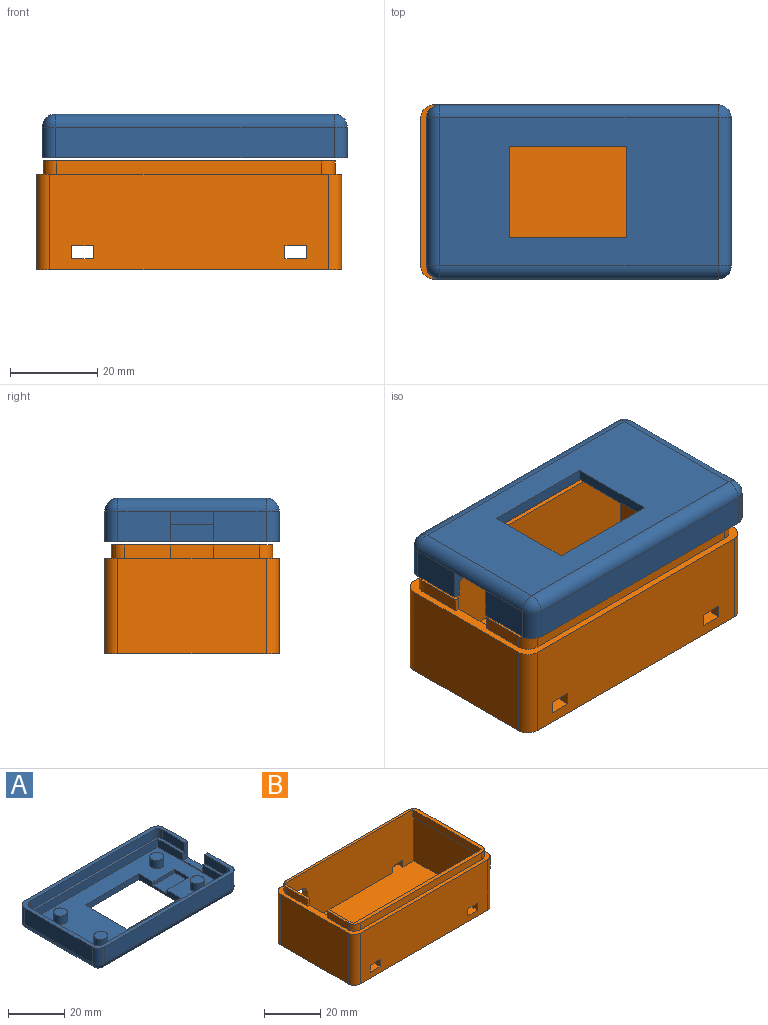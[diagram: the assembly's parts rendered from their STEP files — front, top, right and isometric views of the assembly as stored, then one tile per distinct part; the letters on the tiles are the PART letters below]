
ASSEMBLY  parts=2 mates=1
PART A: 53 faces, bbox 70x40x10 mm
  f0: plane 70x40mm, normal (0,0,1), area 293.4mm2, adj f9,f10,f11,f15,f16,f17,f18,f26
  f1: plane 35x3.5mm, normal (1,0,0), area 122.5mm2, adj f2,f4,f12,f39
  f2: plane 65x3.5mm, normal (0,1,0), area 227.5mm2, adj f1,f3,f12,f39
  f3: plane 35x3.5mm, normal (-1,0,0), area 92.5mm2, adj f2,f4,f9,f10,f12,f38,f39
  f4: plane 65x3.5mm, normal (0,-1,0), area 227.5mm2, adj f1,f3,f12,f39
  f5: cylinder r=2.5mm len=5mm, axis (0,0,-1), area 55mm2, adj f12,f52
  f6: cylinder r=2.5mm len=5mm, axis (0,0,-1), area 55mm2, adj f12,f51
  f7: cylinder r=2.5mm len=5mm, axis (0,0,-1), area 55mm2, adj f12,f50
  f8: cylinder r=2.5mm len=5mm, axis (0,0,-1), area 55mm2, adj f12,f49
  f9: plane 7x2.5mm, normal (0,1,0), area 13.1mm2, adj f0,f3,f11,f38,f39,f41
  f10: plane 7x2.5mm, normal (0,-1,0), area 13.1mm2, adj f0,f3,f17,f38,f39,f40
  f11: plane 12x7mm, normal (1,0,0), area 84mm2, adj f0,f9,f28,f29
  f12: plane 65x35mm, normal (0,0,1), area 1552.5mm2, adj f1,f2,f3,f4,f5,f6,f7,f8
  f13: plane 21x2.5mm, normal (-1,0,0), area 42mm2, adj f12,f14,f19,f21,f22,f23,f25
  f14: plane 64x34mm, normal (0,0,-1), area 1609mm2, adj f13,f19,f20,f21,f29,f30,f34,f35
  f15: plane 34x7mm, normal (-1,0,0), area 238mm2, adj f0,f31,f35,f37
  f16: plane 64x7mm, normal (0,-1,0), area 448mm2, adj f0,f28,f34,f37
  f17: plane 12x7mm, normal (1,0,0), area 84mm2, adj f0,f10,f26,f29
  f18: plane 64x7mm, normal (0,1,0), area 448mm2, adj f0,f26,f30,f31
  f19: plane 27x2.5mm, normal (0,-1,0), area 67.5mm2, adj f12,f13,f14,f20
  f20: plane 21x2.5mm, normal (1,0,0), area 52.5mm2, adj f12,f14,f19,f21
  f21: plane 27x2.5mm, normal (0,1,0), area 67.5mm2, adj f12,f13,f14,f20
  f22: plane 11x1.5mm, normal (0,-1,0), area 16.5mm2, adj f12,f13,f24,f25
  f23: plane 11x1.5mm, normal (0,1,0), area 16.5mm2, adj f12,f13,f24,f25
  f24: plane 7x1.5mm, normal (-1,0,0), area 10.5mm2, adj f12,f22,f23,f25
  f25: plane 11x7mm, normal (0,0,1), area 77mm2, adj f13,f22,f23,f24
  f26: cylinder r=3mm len=7mm, axis (0,0,1), area 33mm2, adj f0,f17,f18,f27
  f27: sphere r=3mm, area 14.1mm2, adj f26,f29,f30
  f28: cylinder r=3mm len=7mm, axis (0,0,-1), area 33mm2, adj f0,f11,f16,f32
  f29: cylinder r=3mm len=34mm, axis (0,1,0), area 160.2mm2, adj f11,f14,f17,f27,f32,f38
  f30: cylinder r=3mm len=64mm, axis (-1,0,0), area 301.6mm2, adj f14,f18,f27,f33
  f31: cylinder r=3mm len=7mm, axis (0,0,-1), area 33mm2, adj f0,f15,f18,f33
  f32: sphere r=3mm, area 14.1mm2, adj f28,f29,f34
  f33: sphere r=3mm, area 14.1mm2, adj f30,f31,f35
  f34: cylinder r=3mm len=64mm, axis (1,0,0), area 301.6mm2, adj f14,f16,f32,f36
  f35: cylinder r=3mm len=34mm, axis (0,-1,0), area 160.2mm2, adj f14,f15,f33,f36
  f36: sphere r=3mm, area 14.1mm2, adj f34,f35,f37
  f37: cylinder r=3mm len=7mm, axis (0,0,1), area 33mm2, adj f0,f15,f16,f36
  f38: plane 10x2.5mm, normal (0,0,1), area 25mm2, adj f3,f9,f10,f29
  f39: plane 67.1x37.1mm, normal (0,0,1), area 198.9mm2, adj f1,f2,f3,f4,f9,f10,f40,f41
  f40: plane 11.5x4mm, normal (-1,0,0), area 46mm2, adj f0,f10,f39,f48
  f41: plane 11.6x4mm, normal (-1,0,0), area 46.4mm2, adj f0,f9,f39,f42
  f42: cylinder r=2mm len=4mm, axis (0,0,1), area 12.6mm2, adj f0,f39,f41,f43
  f43: plane 63.1x4mm, normal (0,1,0), area 252.4mm2, adj f0,f39,f42,f44
  f44: cylinder r=2mm len=4mm, axis (0,0,1), area 12.6mm2, adj f0,f39,f43,f45
  f45: plane 32.1x4mm, normal (1,0,0), area 128.4mm2, adj f0,f39,f44,f46
  f46: cylinder r=3mm len=4mm, axis (0,0,1), area 18.8mm2, adj f0,f39,f45,f47
  f47: plane 62.1x4mm, normal (0,-1,0), area 248.4mm2, adj f0,f39,f46,f48
  f48: cylinder r=2mm len=4mm, axis (0,0,1), area 12.6mm2, adj f0,f39,f40,f47
  f49: plane 5x5mm, normal (0,0,1), area 19.6mm2, adj f8
  f50: plane 5x5mm, normal (0,0,1), area 19.6mm2, adj f7
  f51: plane 5x5mm, normal (0,0,1), area 19.6mm2, adj f6
  f52: plane 5x5mm, normal (0,0,1), area 19.6mm2, adj f5
PART B: 43 faces, bbox 70x40x25 mm
  f0: plane 10.5x3mm, normal (-1,0,0), area 31.5mm2, adj f1,f6,f28,f42
  f1: plane 67x37mm, normal (0,0,1), area 236mm2, adj f0,f5,f10,f19,f20,f21,f22,f23
  f2: plane 64x22mm, normal (0,-1,0), area 1378mm2, adj f6,f9,f12,f13,f14,f35,f36,f37
  f3: plane 64x22mm, normal (0,1,0), area 1339.5mm2, adj f6,f9,f12,f15,f16,f17,f29,f30
  f4: plane 65x19.5mm, normal (0,1,0), area 1237.5mm2, adj f10,f11,f12,f18,f35,f36,f37,f38
  f5: plane 65x22.5mm, normal (0,-1,0), area 1392.5mm2, adj f1,f10,f11,f12,f17,f18,f27,f29
  f6: plane 70x40mm, normal (0,0,1), area 331mm2, adj f0,f2,f3,f7,f8,f10,f13,f14
  f7: plane 34x22mm, normal (-1,0,0), area 748mm2, adj f6,f9,f13,f16
  f8: plane 34x22mm, normal (1,0,0), area 748mm2, adj f6,f9,f14,f15
  f9: plane 70x40mm, normal (0,0,-1), area 2792.3mm2, adj f2,f3,f7,f8,f13,f14,f15,f16
  f10: plane 35x22.5mm, normal (1,0,0), area 756mm2, adj f1,f4,f5,f6,f12,f18,f26,f41
  f11: plane 35x19.5mm, normal (-1,0,0), area 682.5mm2, adj f4,f5,f12,f18
  f12: plane 65x40mm, normal (0,0,1), area 2325mm2, adj f2,f3,f4,f5,f10,f11,f30,f31
  f13: cylinder r=3mm len=22mm, axis (0,0,1), area 103.7mm2, adj f2,f6,f7,f9
  f14: cylinder r=3mm len=22mm, axis (0,0,-1), area 103.7mm2, adj f2,f6,f8,f9
  f15: cylinder r=3mm len=22mm, axis (0,0,1), area 103.7mm2, adj f3,f6,f8,f9
  f16: cylinder r=3mm len=22mm, axis (0,0,-1), area 103.7mm2, adj f3,f6,f7,f9
  f17: cylinder r=3.5mm len=7mm, axis (0,1,0), area 55mm2, adj f3,f5
  f18: plane 65x35mm, normal (0,0,-1), area 49.7mm2, adj f4,f5,f10,f11,f26,f27
  f19: plane 10.5x3mm, normal (-1,0,0), area 31.5mm2, adj f1,f6,f20,f41
  f20: cylinder r=3mm len=3mm, axis (0,0,-1), area 14.1mm2, adj f1,f6,f19,f21
  f21: plane 61x3mm, normal (0,-1,0), area 183mm2, adj f1,f6,f20,f22
  f22: cylinder r=3mm len=3mm, axis (0,0,-1), area 14.1mm2, adj f1,f6,f21,f23
  f23: plane 31x3mm, normal (1,0,0), area 93mm2, adj f1,f6,f22,f24
  f24: cylinder r=3mm len=3mm, axis (0,0,-1), area 14.1mm2, adj f1,f6,f23,f25
  f25: plane 61x3mm, normal (0,1,0), area 183mm2, adj f1,f6,f24,f28
  f26: plane 64.5x3mm, normal (0,1,0), area 193.5mm2, adj f1,f10,f18,f27
  f27: plane 34.5x3mm, normal (-1,0,0), area 103.5mm2, adj f1,f5,f18,f26
  f28: cylinder r=3mm len=3mm, axis (0,0,-1), area 14.1mm2, adj f0,f1,f6,f25
  f29: plane 5x2.5mm, normal (0,0,-1), area 12.5mm2, adj f3,f5,f30,f31
  f30: plane 3x2.5mm, normal (1,0,0), area 7.5mm2, adj f3,f5,f12,f29
  f31: plane 3x2.5mm, normal (-1,0,0), area 7.5mm2, adj f3,f5,f12,f29
  f32: plane 5x2.5mm, normal (0,0,-1), area 12.5mm2, adj f3,f5,f33,f34
  f33: plane 3x2.5mm, normal (1,0,0), area 7.5mm2, adj f3,f5,f12,f32
  f34: plane 3x2.5mm, normal (-1,0,0), area 7.5mm2, adj f3,f5,f12,f32
  f35: plane 3x2.5mm, normal (-1,0,0), area 7.5mm2, adj f2,f4,f12,f37
  f36: plane 3x2.5mm, normal (1,0,0), area 7.5mm2, adj f2,f4,f12,f37
  f37: plane 5x2.5mm, normal (0,0,-1), area 12.5mm2, adj f2,f4,f35,f36
  f38: plane 3x2.5mm, normal (-1,0,0), area 7.5mm2, adj f2,f4,f12,f40
  f39: plane 3x2.5mm, normal (1,0,0), area 7.5mm2, adj f2,f4,f12,f40
  f40: plane 5x2.5mm, normal (0,0,-1), area 12.5mm2, adj f2,f4,f38,f39
  f41: plane 3x1mm, normal (0,1,0), area 3mm2, adj f1,f6,f10,f19
  f42: plane 3x1mm, normal (0,-1,0), area 3mm2, adj f0,f1,f6,f10
PLACE A rot(axis=(0,1,0),180deg) t=(37.76,23.62,218.06)mm
PLACE B t=(-3.06,3.62,182.3)mm fixed
MATE slider B.f9 <-> A.f14  axis (0,0,-1) through (31.94,23.62,182.3)mm
